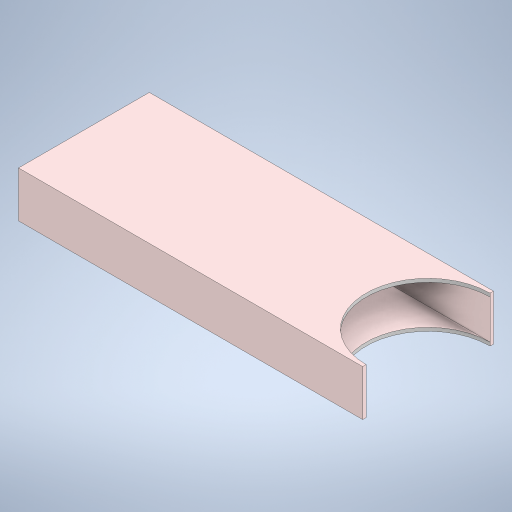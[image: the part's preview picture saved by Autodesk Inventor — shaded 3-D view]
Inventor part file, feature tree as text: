
AUTODESK INVENTOR PART (.ipt)
format: ipt  version: 2024.3 (Build 283343000, 343)  size: 241,664 bytes
history: native  units: mm
features: extrude x2, sketch x2
ambient origin geometry x8: Origin, YZ Plane, XZ Plane, XY Plane, X Axis, Y Axis, Z Axis, Center Point
bodies: Solid1 (feature_tree)
feature tree (4):
  extrude  "Extrusion1"  Depth=40.0mm
  extrude  "Extrusion2"  Depth=3.0mm
  sketch  "Sketch1"  dims[d0=114.0mm d1=40.0mm]
  sketch  "Sketch2"  dims[d2=3.0mm d3=3.0mm d4=300.0mm d5=0.0mm d6=0.0mm d7=0.0mm]
